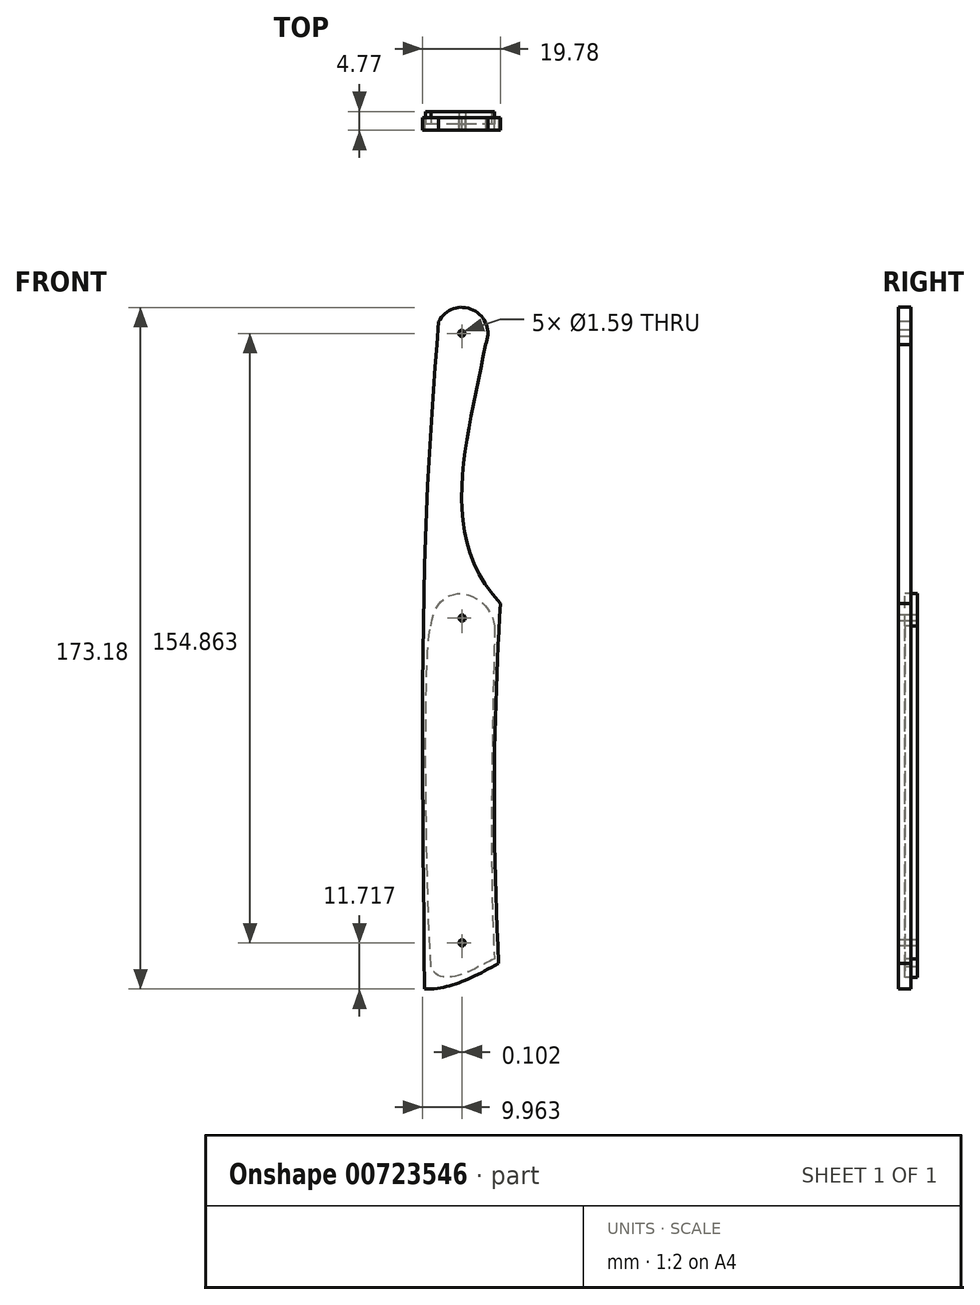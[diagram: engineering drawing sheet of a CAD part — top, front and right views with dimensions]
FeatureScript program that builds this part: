
annotation { "Feature Type Name" : "Feature", "Feature Type Description" : "" }
export const myFeature = defineFeature(function(context is Context, id is Id, definition is map)
    precondition{}
    {
        {
            var Q0;
            Q0=qCreatedBy(makeId("Front.planeOp"),FACE);
            var sketch = newSketch(context, id + "F0", { "sketchPlane" : qUnion([Q0])});
            skLineSegment(sketch, "E0.bottom", {"start": v(-37.67, 57.9) * mm, "end": v(-12.56, 57.9) * mm});
            skLineSegment(sketch, "E0.top", {"start": v(-37.67, -120.4) * mm, "end": v(-12.56, -120.4) * mm});
            skLineSegment(sketch, "E0.left", {"start": v(-37.67, 57.9) * mm, "end": v(-37.67, -120.4) * mm});
            skLineSegment(sketch, "E0.right", {"start": v(-12.56, 57.9) * mm, "end": v(-12.56, -120.4) * mm});
            skFitSpline(sketch, "E1", {"points": [v(-34.35, -116.48) * mm, v(-34.35, -7.97) * mm, v(-30.82, 53.02) * mm], "startDerivative": vector(-2.35, 203.54) * mm, "endDerivative": vector(10, 132.07) * mm});
            skArc(sketch, "E2", {"start": v(-18.94, 47.25) * mm, "mid": v(-22.02, 56.02) * mm, "end": v(-30.82, 53.02) * mm});
            skFitSpline(sketch, "E3", {"points": [v(-18.94, 47.25) * mm, v(-15.09, -18.56) * mm], "startDerivative": vector(-11.56, -69.34) * mm, "endDerivative": vector(51.04, -55.7) * mm});
            skFitSpline(sketch, "E4", {"points": [v(-15.53, -110) * mm, v(-15.09, -18.56) * mm], "startDerivative": vector(-5.54, 102.17) * mm, "endDerivative": vector(4.92, 79.65) * mm});
            skFitSpline(sketch, "E5", {"points": [v(-15.53, -110) * mm, v(-34.35, -116.48) * mm], "startDerivative": vector(-21.33, -11.64) * mm, "endDerivative": vector(-18.89, 0.78) * mm});
            skCircle(sketch, "E6", {"center": v(-24.9, 50.08) * mm, "radius": 0.8 * mm});
            skPoint(sketch, "E7", {"position": v(-24.9, 56.02) * mm});
            skPoint(sketch, "E7.positionSnap0", {"position": v(-22.02, 56.02) * mm});
            skPoint(sketch, "E8", {"position": v(-34.6, -18.56) * mm});
            skSolve(sketch);
        }
        {
            var Q0;
            Q0=makeQuery(id+"F0.imprint","IMPRINT",FACE,{"disambiguationData":[TD([[makeQuery(id+"F0.imprint","IMPRINT",EDGE,{"derivedFrom":sQuery(id+"F0.wireOp",EDGE,"E1")}),-1.0]])]});
            extrude(context, id + "F1", {"entities" : qUnion([Q0]), "endBound" : BoundingType.SYMMETRIC, "oppositeDirection" : true, "depth" : 3.17 * mm, "offsetDistance" : 25.4 * mm});
        }
        {
            var Q0;
            Q0=qCreatedBy(makeId("Front.planeOp"),FACE);
            var sketch = newSketch(context, id + "F2", { "sketchPlane" : qUnion([Q0])});
            skFitSpline(sketch, "E9", {"points": [v(-16.6, -108.9) * mm, v(-32.75, -110.87) * mm], "startDerivative": vector(-12.7, -5.56) * mm, "endDerivative": vector(-7.3, 18.53) * mm});
            skFitSpline(sketch, "E10", {"points": [v(-32.75, -110.87) * mm, v(-32.75, -24.26) * mm], "startDerivative": vector(-4.77, 85.78) * mm, "endDerivative": vector(5.78, 14.96) * mm});
            skFitSpline(sketch, "E11", {"points": [v(-32.75, -24.26) * mm, v(-16.6, -24.26) * mm], "startDerivative": vector(4.77, 38.13) * mm, "endDerivative": vector(3.97, -27) * mm});
            skFitSpline(sketch, "E12", {"points": [v(-16.6, -24.26) * mm, v(-16.6, -108.9) * mm], "startDerivative": vector(0, -24.2) * mm, "endDerivative": vector(5.05, -82) * mm});
            skSolve(sketch);
        }
        {
            var Q0;
            Q0=qSketchRegion(id+"F2",true);
            extrude(context, id + "F3", {"entities" : qUnion([Q0]), "oppositeDirection" : true, "depth" : 3.17 * mm, "offsetDistance" : 25.4 * mm});
        }
        {
            var Q0;
            Q0=makeQuery(id+"F1.opExtrude","CAP_FACE",FACE,{"disambiguationData":[OSD([sQuery(id+"F0.wireOp",EDGE,"E1"),sQuery(id+"F0.wireOp",EDGE,"E2"),sQuery(id+"F0.wireOp",EDGE,"E3"),sQuery(id+"F0.wireOp",EDGE,"E4"),sQuery(id+"F0.wireOp",EDGE,"E5"),sQuery(id+"F0.wireOp",EDGE,"E6")])],"isStart":false});
            var sketch = newSketch(context, id + "F4", { "sketchPlane" : qUnion([Q0])});
            skCircle(sketch, "E13", {"center": v(24.8, -22.25) * mm, "radius": 0.8 * mm});
            skCircle(sketch, "E14", {"center": v(24.81, -104.78) * mm, "radius": 0.8 * mm});
            skSolve(sketch);
        }
        {
            var Q0;
            Q0=qSketchRegion(id+"F4",true);
            extrude(context, id + "F5", {"entities" : qUnion([Q0]), "operationType" : NewBodyOperationType.REMOVE, "endBound" : BoundingType.SYMMETRIC, "depth" : 25.4 * mm, "offsetDistance" : 25.4 * mm});
        }
    });
